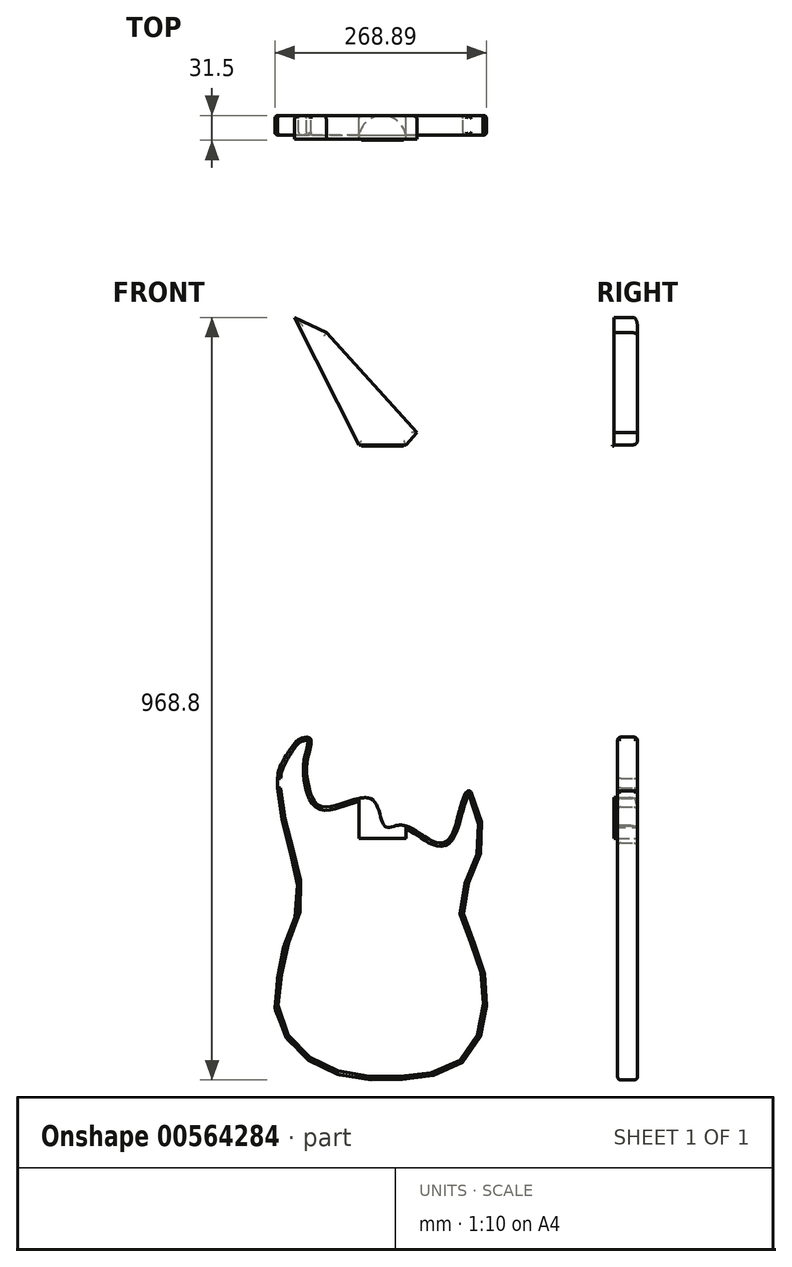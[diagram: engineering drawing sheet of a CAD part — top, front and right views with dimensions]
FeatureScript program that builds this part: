
annotation { "Feature Type Name" : "Feature", "Feature Type Description" : "" }
export const myFeature = defineFeature(function(context is Context, id is Id, definition is map)
    precondition{}
    {
        {
            var Q0;
            Q0=qCreatedBy(makeId("Front.planeOp"),FACE);
            var sketch = newSketch(context, id + "F0", { "sketchPlane" : qUnion([Q0])});
            skLineSegment(sketch, "E0.left", {"start": v(-145.12, 209.06) * mm, "end": v(-145.12, 197.04) * mm});
            skFitSpline(sketch, "E1", {"points": [v(-115.89, 259.62) * mm, v(-125.7, 250.97) * mm, v(-138.18, 231.35) * mm, v(-145.12, 209.06) * mm, v(-138.18, 152) * mm, v(-124.8, 101.17) * mm, v(-119.46, 44.99) * mm, v(-135.5, 0) * mm, v(-145.12, -45.96) * mm, v(-145.12, -98.57) * mm, v(-82.9, -161.89) * mm, v(24.1, -172.59) * mm, v(68.43, -163.42) * mm, v(107.04, -131.3) * mm, v(115.5, -28.13) * mm, v(90.54, 40.55) * mm, v(108.57, 103.12) * mm, v(115.5, 143.08) * mm, v(97.97, 193.25) * mm, v(82.96, 156.45) * mm, v(69.58, 129.31) * mm, v(51.75, 129.31) * mm, v(12.03, 149.67) * mm, v(-8.57, 147.97) * mm, v(-26.1, 182.78) * mm, v(-87.36, 172.75) * mm, v(-106.18, 201.54) * mm, v(-106.97, 234.03) * mm, v(-103.4, 259.62) * mm, v(-115.89, 259.62) * mm]});
            skLineSegment(sketch, "E2.bottom", {"start": v(-41.76, 132.78) * mm, "end": v(18.04, 132.78) * mm});
            skLineSegment(sketch, "E2.top", {"start": v(-41.76, 632.78) * mm, "end": v(18.04, 632.78) * mm});
            skLineSegment(sketch, "E2.left", {"start": v(-41.76, 132.78) * mm, "end": v(-41.76, 632.78) * mm});
            skLineSegment(sketch, "E2.right", {"start": v(18.04, 132.78) * mm, "end": v(18.04, 632.78) * mm});
            skLineSegment(sketch, "E3", {"start": v(-41.76, 632.78) * mm, "end": v(-123.66, 794.6) * mm});
            skLineSegment(sketch, "E4", {"start": v(-123.66, 794.6) * mm, "end": v(-83.17, 775.05) * mm});
            skLineSegment(sketch, "E5", {"start": v(-83.17, 775.05) * mm, "end": v(32, 648.36) * mm});
            skLineSegment(sketch, "E6", {"start": v(32, 648.36) * mm, "end": v(18.04, 632.78) * mm});
            skSolve(sketch);
        }
        {
            var Q0;
            {var subQ0=sQuery(id+"F0.wireOp",EDGE,"E0.left");Q0=makeQuery(id+"F0.imprint","IMPRINT",FACE,{"disambiguationData":[TD([[makeQuery(id+"F0.imprint","IMPRINT",EDGE,{"derivedFrom":subQ0}),1.0]])]});}
            extrude(context, id + "F1", {"entities" : qUnion([Q0]), "depth" : 25 * mm, "offsetDistance" : 25 * mm});
        }
        {
            var Q0;
            {var subQ4=sQuery(id+"F0.wireOp",EDGE,"E2.bottom");Q0=makeQuery(id+"F0.imprint","IMPRINT",FACE,{"disambiguationData":[TD([[makeQuery(id+"F0.imprint","IMPRINT",EDGE,{"derivedFrom":subQ4}),1.0]])]});}
            extrude(context, id + "F2", {"entities" : qUnion([Q0]), "depth" : 30 * mm, "offsetDistance" : 25 * mm});
        }
        {
            var Q0;
            Q0=makeQuery(id+"F2.opExtrude","CAP_EDGE",EDGE,{"disambiguationData":[OSD([sQuery(id+"F0.wireOp",EDGE,"E2.left")])],"isStart":false});
            var Q1;
            Q1=makeQuery(id+"F2.opExtrude","CAP_EDGE",EDGE,{"disambiguationData":[OSD([sQuery(id+"F0.wireOp",EDGE,"E2.right")])],"isStart":false});
            fillet(context, id + "F3", {"entities" : qUnion([Q0, Q1]), "radius" : 3 * mm, "tangentPropagation" : true, "allowEdgeOverflow" : false});
        }
        {
            var Q0;
            {var subQ0=sQuery(id+"F0.wireOp",EDGE,"E1");Q0=makeQuery(id+"F1.opExtrude","CAP_EDGE",EDGE,{"disambiguationData":[OSD([subQ0]),TDD([makeQuery(id+"F0.imprint","IMPRINT",EDGE,{"disambiguationData":[TD([[makeQuery(id+"F0.imprint","INTERSECT",VERTEX,{"disambiguationData":[OD(1.0)],"derivedFrom":[sQuery(id+"F0.wireOp",EDGE,"E0.left"),subQ0]}),-1.0]])],"derivedFrom":subQ0})])],"isStart":false});}
            var Q1;
            Q1=makeQuery(id+"F1.opExtrude","CAP_EDGE",EDGE,{"disambiguationData":[OSD([sQuery(id+"F0.wireOp",EDGE,"E0.left")])],"isStart":false});
            var Q2;
            {var subQ0=sQuery(id+"F0.wireOp",EDGE,"E1");Q2=makeQuery(id+"F1.opExtrude","CAP_EDGE",EDGE,{"disambiguationData":[OSD([subQ0]),TDD([makeQuery(id+"F0.imprint","IMPRINT",EDGE,{"disambiguationData":[TD([[makeQuery(id+"F0.imprint","INTERSECT",VERTEX,{"disambiguationData":[OD(0.0)],"derivedFrom":[sQuery(id+"F0.wireOp",EDGE,"E0.left"),subQ0]}),1.0]])],"derivedFrom":subQ0})])],"isStart":false});}
            var Q3;
            {var subQ0=sQuery(id+"F0.wireOp",EDGE,"E1");Q3=makeQuery(id+"F1.opExtrude","CAP_EDGE",EDGE,{"disambiguationData":[OSD([subQ0]),TDD([makeQuery(id+"F0.imprint","IMPRINT",EDGE,{"disambiguationData":[TD([[makeQuery(id+"F0.imprint","INTERSECT",VERTEX,{"disambiguationData":[OD(1.0)],"derivedFrom":[sQuery(id+"F0.wireOp",EDGE,"E0.left"),subQ0]}),-1.0]])],"derivedFrom":subQ0})])],"isStart":true});}
            var Q4;
            {var subQ0=sQuery(id+"F0.wireOp",EDGE,"E1");Q4=makeQuery(id+"F1.opExtrude","CAP_EDGE",EDGE,{"disambiguationData":[OSD([subQ0]),TDD([makeQuery(id+"F0.imprint","IMPRINT",EDGE,{"disambiguationData":[TD([[makeQuery(id+"F0.imprint","INTERSECT",VERTEX,{"disambiguationData":[OD(0.0)],"derivedFrom":[sQuery(id+"F0.wireOp",EDGE,"E0.left"),subQ0]}),1.0]])],"derivedFrom":subQ0})])],"isStart":true});}
            var Q5;
            Q5=makeQuery(id+"F1.opExtrude","CAP_EDGE",EDGE,{"disambiguationData":[OSD([sQuery(id+"F0.wireOp",EDGE,"E0.left")])],"isStart":true});
            fillet(context, id + "F4", {"entities" : qUnion([Q0, Q1, Q2, Q3, Q4, Q5]), "radius" : 4 * mm, "tangentPropagation" : true, "allowEdgeOverflow" : false});
        }
        {
            var Q0;
            Q0=makeQuery(id+"F2.opExtrude","CAP_EDGE",EDGE,{"disambiguationData":[OSD([sQuery(id+"F0.wireOp",EDGE,"E2.left")])],"isStart":true});
            var Q1;
            Q1=makeQuery(id+"F2.opExtrude","CAP_EDGE",EDGE,{"disambiguationData":[OSD([sQuery(id+"F0.wireOp",EDGE,"E2.right")])],"isStart":true});
            fillet(context, id + "F5", {"entities" : qUnion([Q0, Q1]), "radius" : 30 * mm, "tangentPropagation" : true, "allowEdgeOverflow" : false});
        }
        {
            var Q0;
            Q0=makeQuery(id+"F0.imprint","IMPRINT",FACE,{"disambiguationData":[TD([[makeQuery(id+"F0.imprint","IMPRINT",EDGE,{"derivedFrom":sQuery(id+"F0.wireOp",EDGE,"E2.top")}),1.0]])]});
            extrude(context, id + "F6", {"entities" : qUnion([Q0]), "operationType" : NewBodyOperationType.ADD, "depth" : 30 * mm, "offsetDistance" : 25 * mm});
        }
        {
            var Q0;
            {var subQ0=sQuery(id+"F0.wireOp",EDGE,"E2.right");var subQ2=sQuery(id+"F0.wireOp",EDGE,"E2.top");Q0=makeQuery(id+"F6.boolean.opBoolean","SPLIT",EDGE,{"disambiguationData":[TD([makeQuery(id+"F5.opFillet","BLEND_FACE",FACE,{"disambiguationData":[OSD([subQ0])]})])],"derivedFrom":makeQuery(id+"F6.opExtrude","CAP_EDGE",EDGE,{"disambiguationData":[OSD([subQ2])],"isStart":true})});}
            var Q1;
            Q1=makeQuery(id+"F6.opExtrude","CAP_EDGE",EDGE,{"disambiguationData":[OSD([sQuery(id+"F0.wireOp",EDGE,"E6")])],"isStart":true});
            var Q2;
            {var subQ0=sQuery(id+"F0.wireOp",EDGE,"E2.left");var subQ2=sQuery(id+"F0.wireOp",EDGE,"E2.top");Q2=makeQuery(id+"F6.boolean.opBoolean","SPLIT",EDGE,{"disambiguationData":[TD([makeQuery(id+"F5.opFillet","BLEND_FACE",FACE,{"disambiguationData":[OSD([subQ0])]})])],"derivedFrom":makeQuery(id+"F6.opExtrude","CAP_EDGE",EDGE,{"disambiguationData":[OSD([subQ2])],"isStart":true})});}
            var Q3;
            Q3=makeQuery(id+"F6.opExtrude","CAP_EDGE",EDGE,{"disambiguationData":[OSD([sQuery(id+"F0.wireOp",EDGE,"E3")])],"isStart":true});
            var Q4;
            Q4=makeQuery(id+"F6.opExtrude","CAP_EDGE",EDGE,{"disambiguationData":[OSD([sQuery(id+"F0.wireOp",EDGE,"E5")])],"isStart":true});
            var Q5;
            Q5=makeQuery(id+"F6.opExtrude","CAP_EDGE",EDGE,{"disambiguationData":[OSD([sQuery(id+"F0.wireOp",EDGE,"E4")])],"isStart":true});
            fillet(context, id + "F7", {"entities" : qUnion([Q0, Q1, Q2, Q3, Q4, Q5]), "radius" : 5 * mm, "tangentPropagation" : true, "allowEdgeOverflow" : false});
        }
        {
            var Q0;
            {var subQ0=sQuery(id+"F0.wireOp",EDGE,"E2.top");Q0=makeQuery(id+"F6.boolean.opBoolean","MERGE",FACE,{"derivedFrom":[makeQuery(id+"F2.opExtrude","CAP_FACE",FACE,{"disambiguationData":[OSD([sQuery(id+"F0.wireOp",EDGE,"E2.bottom"),subQ0,sQuery(id+"F0.wireOp",EDGE,"E2.left"),sQuery(id+"F0.wireOp",EDGE,"E2.right")])],"isStart":false}),makeQuery(id+"F6.opExtrude","CAP_FACE",FACE,{"disambiguationData":[OSD([subQ0,sQuery(id+"F0.wireOp",EDGE,"E3"),sQuery(id+"F0.wireOp",EDGE,"E4"),sQuery(id+"F0.wireOp",EDGE,"E5"),sQuery(id+"F0.wireOp",EDGE,"E6")])],"isStart":false})]});}
            var sketch = newSketch(context, id + "F8", { "sketchPlane" : qUnion([Q0])});
            skLineSegment(sketch, "E7.bottom", {"start": v(-38.76, 632.78) * mm, "end": v(15.04, 632.78) * mm});
            skLineSegment(sketch, "E7.top", {"start": v(-38.76, 631.28) * mm, "end": v(15.04, 631.28) * mm});
            skLineSegment(sketch, "E7.left", {"start": v(-38.76, 632.78) * mm, "end": v(-38.76, 631.28) * mm});
            skLineSegment(sketch, "E7.right", {"start": v(15.04, 632.78) * mm, "end": v(15.04, 631.28) * mm});
            skSolve(sketch);
        }
        {
            var Q0;
            Q0=makeQuery(id+"F8.imprint","IMPRINT",FACE,{"disambiguationData":[TD([[makeQuery(id+"F8.imprint","IMPRINT",EDGE,{"derivedFrom":sQuery(id+"F8.wireOp",EDGE,"E7.bottom")}),-1.0]])]});
            extrude(context, id + "F9", {"entities" : qUnion([Q0]), "operationType" : NewBodyOperationType.ADD, "depth" : 1.5 * mm, "offsetDistance" : 25 * mm});
        }
    });
